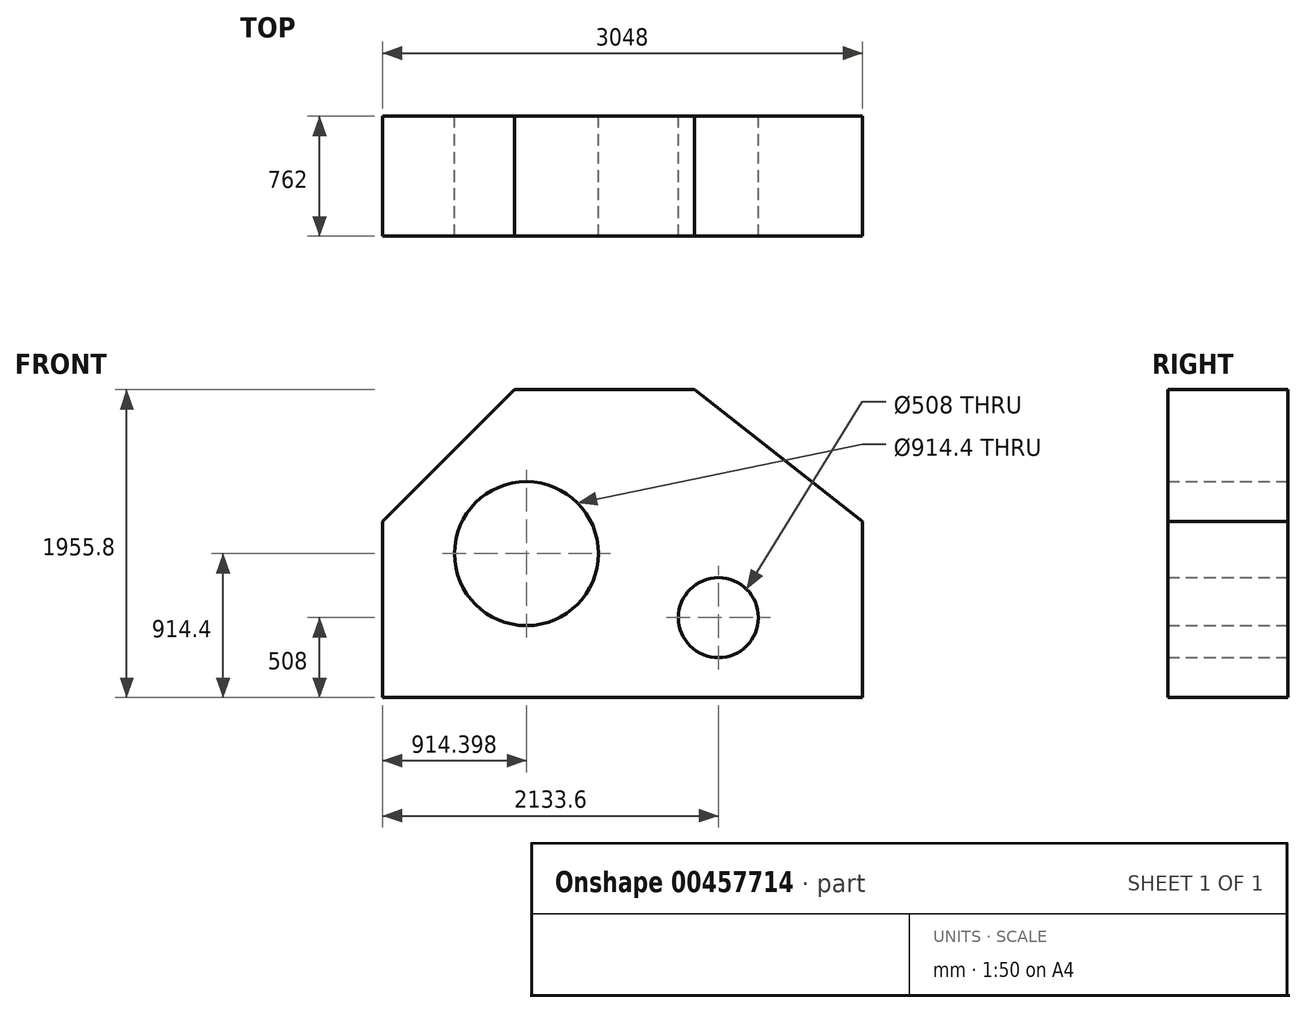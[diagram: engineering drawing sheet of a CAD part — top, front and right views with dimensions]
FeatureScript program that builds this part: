
annotation { "Feature Type Name" : "Feature", "Feature Type Description" : "" }
export const myFeature = defineFeature(function(context is Context, id is Id, definition is map)
    precondition{}
    {
        {
            var Q0;
            Q0=qCreatedBy(makeId("Front.planeOp"),FACE);
            var sketch = newSketch(context, id + "F0", { "sketchPlane" : qUnion([Q0])});
            skLineSegment(sketch, "E0", {"start": v(-63.54, 203.2) * mm, "end": v(-63.54, -914.4) * mm});
            skLineSegment(sketch, "E1", {"start": v(-63.54, -914.4) * mm, "end": v(2984.46, -914.4) * mm});
            skLineSegment(sketch, "E2", {"start": v(-63.54, 203.2) * mm, "end": v(774.66, 1041.4) * mm});
            skLineSegment(sketch, "E3", {"start": v(774.66, 1041.4) * mm, "end": v(1917.66, 1041.4) * mm});
            skLineSegment(sketch, "E4", {"start": v(2984.46, -914.4) * mm, "end": v(2984.46, 203.2) * mm});
            skLineSegment(sketch, "E5", {"start": v(1917.66, 1041.4) * mm, "end": v(2984.46, 203.2) * mm});
            skCircle(sketch, "E6", {"center": v(2070.06, -406.4) * mm, "radius": 254 * mm});
            skCircle(sketch, "E7", {"center": v(850.86, 0) * mm, "radius": 457.2 * mm});
            skSolve(sketch);
        }
        {
            var Q0;
            Q0=makeQuery(id+"F0.imprint","IMPRINT",FACE,{"disambiguationData":[TD([[makeQuery(id+"F0.imprint","IMPRINT",EDGE,{"derivedFrom":sQuery(id+"F0.wireOp",EDGE,"E0")}),1.0]])]});
            extrude(context, id + "F1", {"entities" : qUnion([Q0]), "depth" : 762 * mm});
        }
    });
